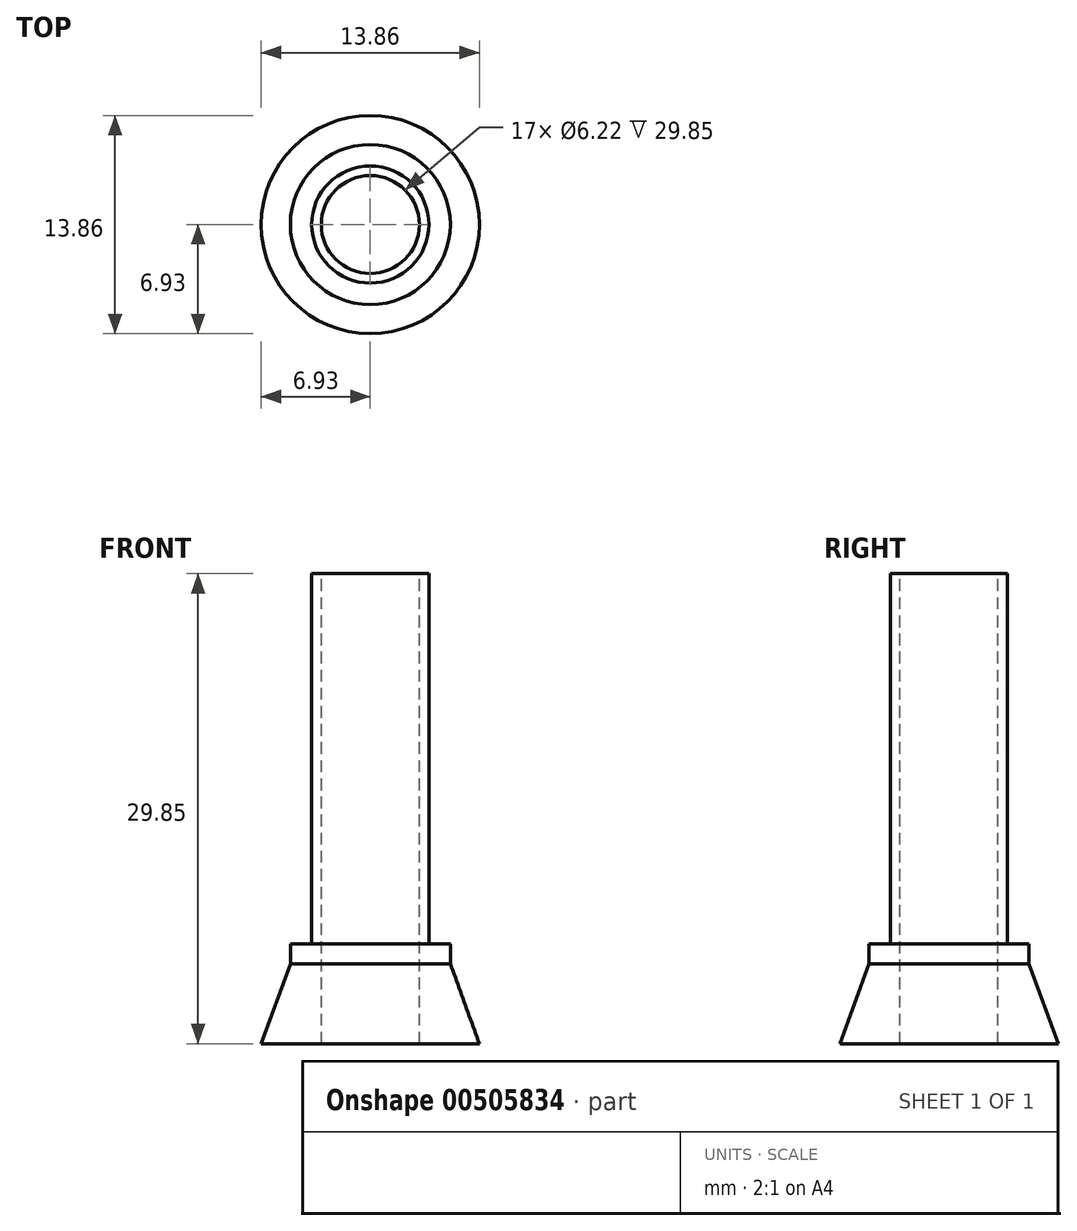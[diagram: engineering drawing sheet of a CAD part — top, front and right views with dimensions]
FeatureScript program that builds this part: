
annotation { "Feature Type Name" : "Feature", "Feature Type Description" : "" }
export const myFeature = defineFeature(function(context is Context, id is Id, definition is map)
    precondition{}
    {
        {
            var Q0;
            Q0=qCreatedBy(makeId("Front.planeOp"),FACE);
            var sketch = newSketch(context, id + "F0", { "sketchPlane" : qUnion([Q0])});
            skLineSegment(sketch, "E0", {"start": v(3.11, 0) * mm, "end": v(3.11, 29.85) * mm});
            skLineSegment(sketch, "E1", {"start": v(3.11, 29.85) * mm, "end": v(3.72, 29.85) * mm});
            skLineSegment(sketch, "E2", {"start": v(3.72, 29.85) * mm, "end": v(3.72, 6.35) * mm});
            skLineSegment(sketch, "E3", {"start": v(3.72, 6.35) * mm, "end": v(5.08, 6.35) * mm});
            skLineSegment(sketch, "E4", {"start": v(5.08, 6.35) * mm, "end": v(5.08, 5.08) * mm});
            skLineSegment(sketch, "E5.MirrorCS", {"start": v(-5.08, 0) * mm, "end": v(-3.11, 0) * mm});
            skLineSegment(sketch, "E6.MirrorCS", {"start": v(-5.08, 6.35) * mm, "end": v(-5.08, 0) * mm});
            skLineSegment(sketch, "E7.MirrorCS", {"start": v(-3.72, 6.35) * mm, "end": v(-5.08, 6.35) * mm});
            skLineSegment(sketch, "E8.MirrorCS", {"start": v(-3.72, 29.85) * mm, "end": v(-3.72, 6.35) * mm});
            skLineSegment(sketch, "E9.MirrorCS", {"start": v(-3.11, 0) * mm, "end": v(-3.11, 29.85) * mm});
            skLineSegment(sketch, "E10.MirrorCS", {"start": v(-3.11, 29.85) * mm, "end": v(-3.72, 29.85) * mm});
            skLineSegment(sketch, "E11", {"start": v(0, 0) * mm, "end": v(0, 36.2) * mm, "construction": true});
            skLineSegment(sketch, "E12", {"start": v(5.08, 5.08) * mm, "end": v(6.93, 0) * mm});
            skLineSegment(sketch, "E13", {"start": v(3.11, 0) * mm, "end": v(6.93, 0) * mm});
            skLineSegment(sketch, "E14", {"start": v(-3.72, 6.35) * mm, "end": v(3.72, 6.35) * mm, "construction": true});
            skSolve(sketch);
        }
        {
            var Q0;
            Q0=sQuery(id+"F0.wireOp",EDGE,"E13");
            var Q1;
            Q1=sQuery(id+"F0.wireOp",EDGE,"E12");
            var Q2;
            Q2=sQuery(id+"F0.wireOp",EDGE,"E4");
            var Q3;
            Q3=sQuery(id+"F0.wireOp",EDGE,"E0");
            var Q4;
            Q4=sQuery(id+"F0.wireOp",EDGE,"E2");
            var Q5;
            Q5=sQuery(id+"F0.wireOp",EDGE,"E1");
            var Q6;
            Q6=sQuery(id+"F0.wireOp",EDGE,"E11");
            revolve(context, id + "F1", {"bodyType" : ToolBodyType.SURFACE, "surfaceEntities" : qUnion([Q0, Q1, Q2, Q3, Q4, Q5]), "axis" : qUnion([Q6]), "revolveType" : RevolveType.FULL});
        }
    });
